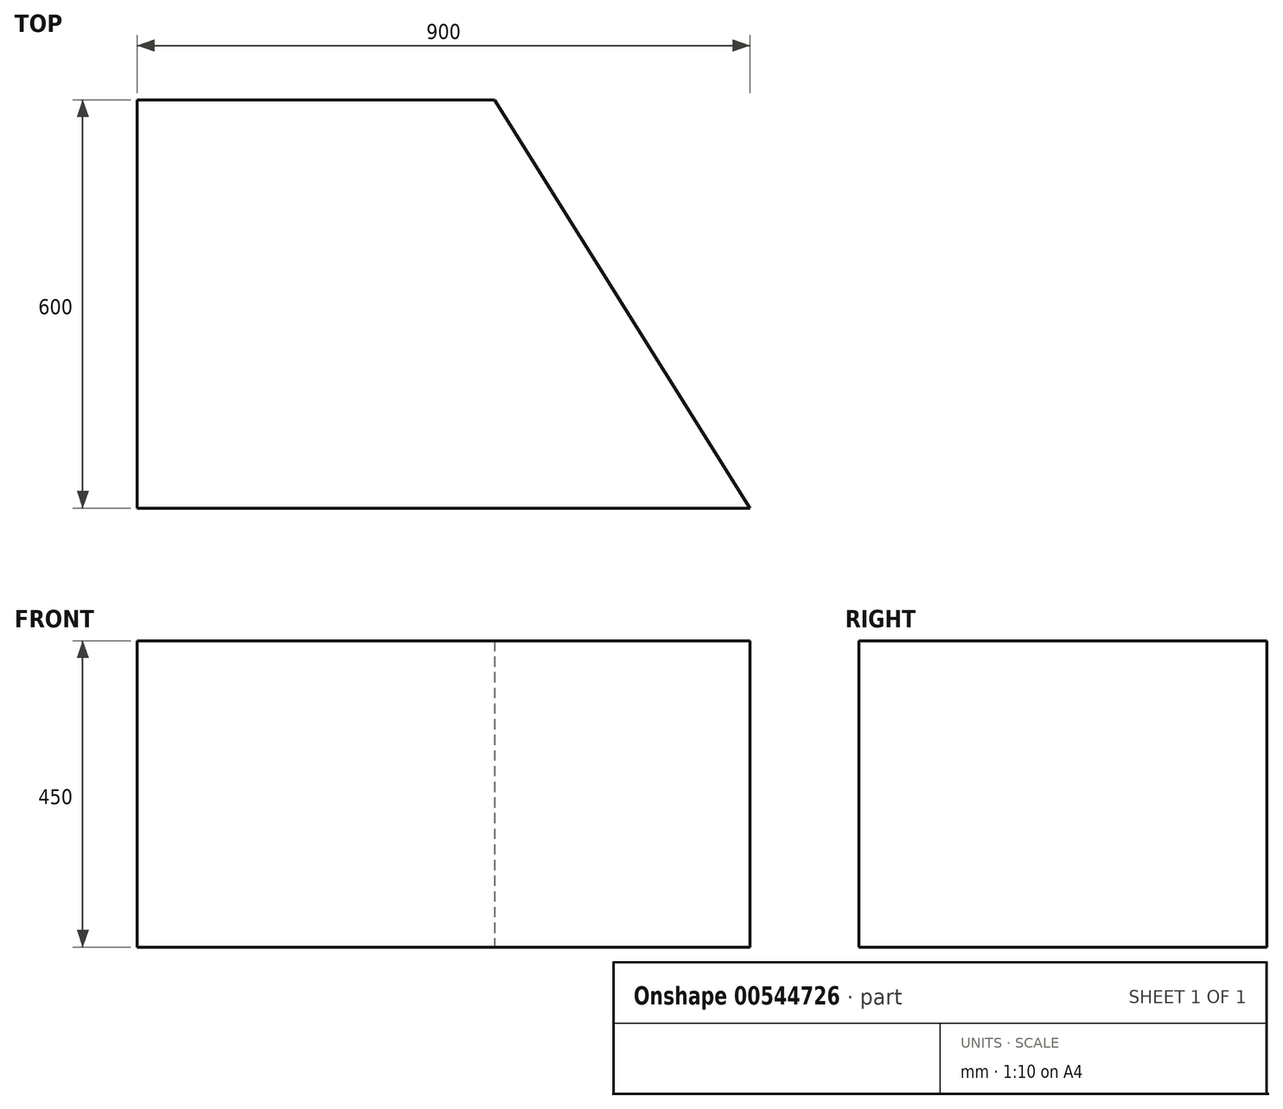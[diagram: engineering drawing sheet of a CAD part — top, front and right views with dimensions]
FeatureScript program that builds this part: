
annotation { "Feature Type Name" : "Feature", "Feature Type Description" : "" }
export const myFeature = defineFeature(function(context is Context, id is Id, definition is map)
    precondition{}
    {
        {
            var Q0;
            Q0=qCreatedBy(makeId("Top.planeOp"),FACE);
            var sketch = newSketch(context, id + "F0", { "sketchPlane" : qUnion([Q0])});
            skLineSegment(sketch, "E0", {"start": v(-545.1, 305.48) * mm, "end": v(504.9, 305.48) * mm});
            skLineSegment(sketch, "E1", {"start": v(504.9, 305.48) * mm, "end": v(879.9, -294.52) * mm});
            skLineSegment(sketch, "E2", {"start": v(879.9, -294.52) * mm, "end": v(-920.1, -294.52) * mm});
            skLineSegment(sketch, "E3", {"start": v(-920.1, -294.52) * mm, "end": v(-545.1, 305.48) * mm});
            skPoint(sketch, "E4", {"position": v(-20.1, 305.48) * mm});
            skPoint(sketch, "E5", {"position": v(-20.1, -294.52) * mm});
            skLineSegment(sketch, "E6", {"start": v(-20.1, -294.52) * mm, "end": v(-20.1, 305.48) * mm});
            skSolve(sketch);
        }
        {
            var Q0;
            {var subQ0=sQuery(id+"F0.wireOp",EDGE,"E1");Q0=makeQuery(id+"F0.imprint","IMPRINT",FACE,{"disambiguationData":[TD([[makeQuery(id+"F0.imprint","IMPRINT",EDGE,{"derivedFrom":subQ0}),-1.0]])]});}
            extrude(context, id + "F1", {"entities" : qUnion([Q0]), "depth" : 450 * mm, "offsetDistance" : 25 * mm});
        }
    });
